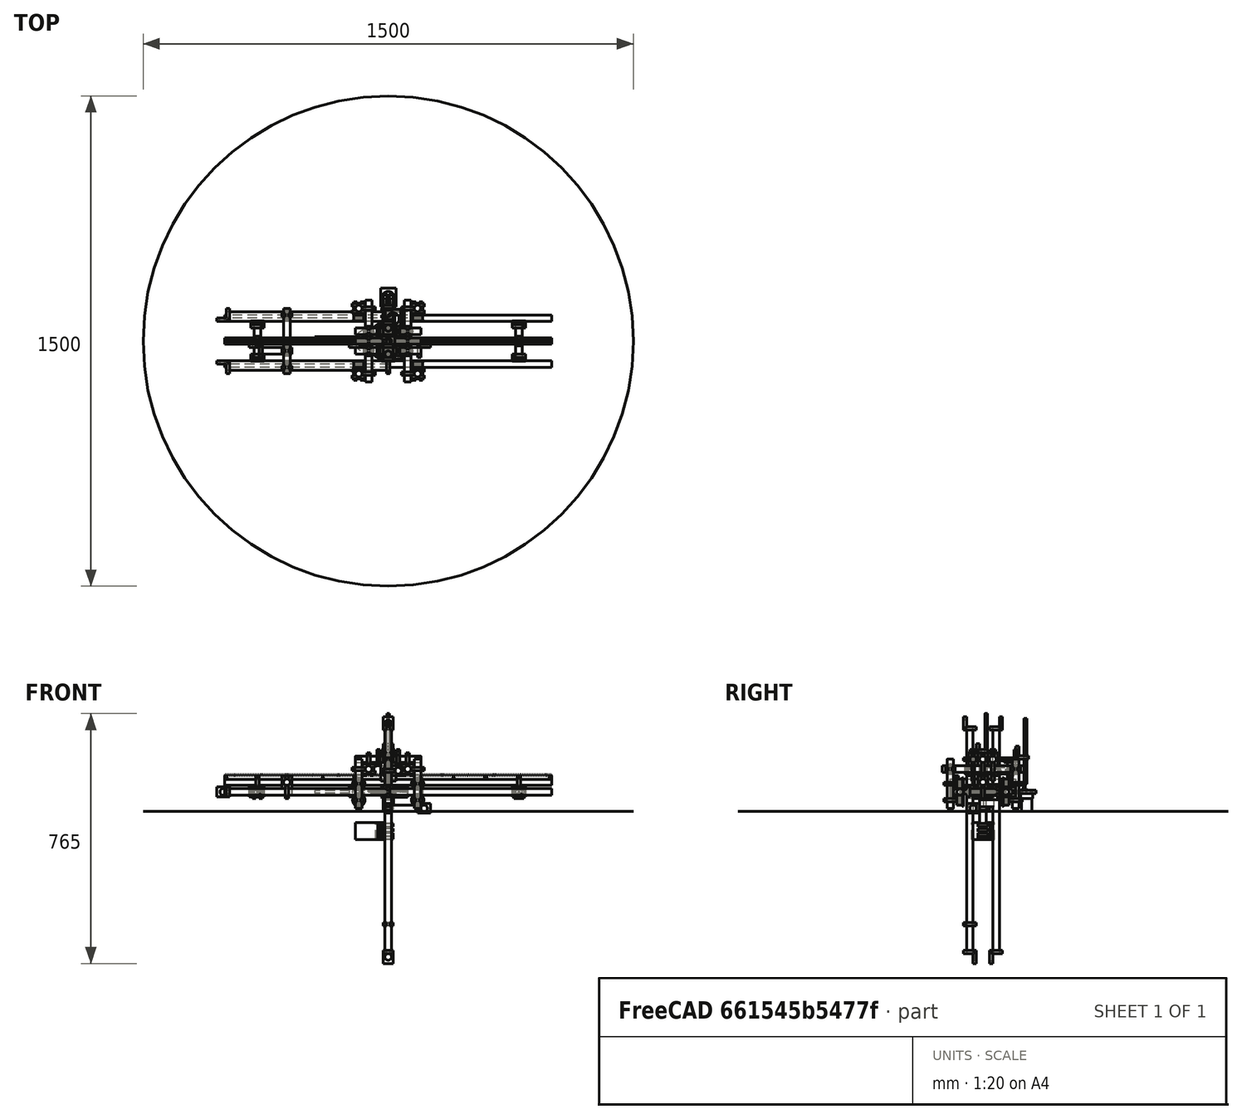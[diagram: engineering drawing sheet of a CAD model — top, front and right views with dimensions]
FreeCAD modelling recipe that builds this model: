
FCSTD DOCUMENT  (FreeCAD 0.17R13522 (Git))
Label: mavis_with_arm_on_1m_rail
License: All rights reserved
LicenseURL: http://en.wikipedia.org/wiki/All_rights_reserved
objects: Part::FeaturePython×50, Part::Cylinder×17, App::DocumentObjectGroup×8, App::Part×8
note: 67 computed .brp shape members not serialized (recipe doc carries the construction recipe); baked Part::Feature solids carry a one-line shape summary decoded from their .brp

FEATURE [Part::FeaturePython] fastener_join_20mm_004  # a2plus imported part (geometry in sourceFile) (typed FeaturePython)
  Placement = pos=(30,-40,65) rot=(0,0.707107,-0.707107;3.14159rad)
  fixedPosition = false
  sourceFile = <userpath>/repo/mavis/parts/fastener-join-20mm.fcstd
  timeLastImport = 1.53614e+09
  updateColors = true
FEATURE [Part::FeaturePython] cogwheel_swivel_01  # a2plus imported part (geometry in sourceFile) (typed FeaturePython)
  fixedPosition = true
  sourceFile = <userpath>/repo/mavis/parts/cogwheel-swivel.fcstd
  timeLastImport = 1.53711e+09
  updateColors = true
FEATURE [Part::FeaturePython] fastener_l_bearing_003  # a2plus imported part (geometry in sourceFile) (typed FeaturePython)
  Placement = pos=(0,-40,195) rot=(0,0,1;1.5708rad)
  fixedPosition = false
  sourceFile = <userpath>/repo/mavis/parts/fastener-l-bearing.fcstd
  timeLastImport = 1.53709e+09
  updateColors = true
FEATURE [Part::FeaturePython] fastener_join_20mm_01  # a2plus imported part (geometry in sourceFile) (typed FeaturePython)
  Placement = pos=(0,85,65) rot=(0,0,1;0rad)
  fixedPosition = false
  sourceFile = <userpath>/repo/mavis/parts/fastener-join-20mm.fcstd
  timeLastImport = 1.53614e+09
  updateColors = true
FEATURE [Part::FeaturePython] fastener_join_20mm_005  # a2plus imported part (geometry in sourceFile) (typed FeaturePython)
  Placement = pos=(30,40,65) rot=(0,0.707107,-0.707107;3.14159rad)
  fixedPosition = false
  sourceFile = <userpath>/repo/mavis/parts/fastener-join-20mm.fcstd
  timeLastImport = 1.53614e+09
  updateColors = true
FEATURE [Part::FeaturePython] fastener_join_20mm_006  # a2plus imported part (geometry in sourceFile) (typed FeaturePython)
  Placement = pos=(0,40,65) rot=(0,0,1;0rad)
  fixedPosition = false
  sourceFile = <userpath>/repo/mavis/parts/fastener-join-20mm.fcstd
  timeLastImport = 1.53614e+09
  updateColors = true
FEATURE [Part::FeaturePython] fastener_l_bearing_005  # a2plus imported part (geometry in sourceFile) (typed FeaturePython)
  Placement = pos=(0,40,195) rot=(0,0,-1;1.5708rad)
  fixedPosition = false
  sourceFile = <userpath>/repo/mavis/parts/fastener-l-bearing.fcstd
  timeLastImport = 1.53709e+09
  updateColors = true
FEATURE [Part::Cylinder] Cylinder003
  Angle = 360
  AttacherType = Attacher::AttachEngine3D
  Height = 200
  Placement = pos=(0,-40,0) rot=(0,0,1;0rad)
  Radius = 10
FEATURE [Part::Cylinder] Cylinder007
  Angle = 360
  AttacherType = Attacher::AttachEngine3D
  Height = 200
  Placement = pos=(0,-40,0) rot=(0,0,1;0rad)
  Radius = 10
FEATURE [Part::Cylinder] Cylinder008
  Angle = 360
  AttacherType = Attacher::AttachEngine3D
  Height = 200
  Placement = pos=(0,40,0) rot=(0,0,1;0rad)
  Radius = 10
FEATURE [Part::Cylinder] Cylinder010
  Angle = 360
  AttacherType = Attacher::AttachEngine3D
  Height = 150
  Placement = pos=(30,-55,65) rot=(-1,0,0;1.5708rad)
  Radius = 10
FEATURE [Part::FeaturePython] fastener_join_20mm_007  # a2plus imported part (geometry in sourceFile) (typed FeaturePython)
  Placement = pos=(0,-40,65) rot=(0,0,1;0rad)
  fixedPosition = false
  sourceFile = <userpath>/repo/mavis/parts/fastener-join-20mm.fcstd
  timeLastImport = 1.53614e+09
  updateColors = true
FEATURE [Part::FeaturePython] fastener_join_20mm_011  # a2plus imported part (geometry in sourceFile) (typed FeaturePython)
  Placement = pos=(30,85,65) rot=(0,0.707107,-0.707107;3.14159rad)
  fixedPosition = false
  sourceFile = <userpath>/repo/mavis/parts/fastener-join-20mm.fcstd
  timeLastImport = 1.53614e+09
  updateColors = true
FEATURE [Part::Cylinder] Cylinder011
  Angle = 360
  AttacherType = Attacher::AttachEngine3D
  Height = 50
  Placement = pos=(0,85,50) rot=(0,0,1;0rad)
  Radius = 10
FEATURE [Part::FeaturePython] fastener_l_bearing_006  # a2plus imported part (geometry in sourceFile) (typed FeaturePython)
  Placement = pos=(0,85,95) rot=(0,0,-1;1.5708rad)
  fixedPosition = false
  sourceFile = <userpath>/repo/mavis/parts/fastener-l-bearing.fcstd
  timeLastImport = 1.53709e+09
  updateColors = true
FEATURE [App::DocumentObjectGroup] Group001  label="BaseParts"
  Group = -> [fastener_l_bearing_006,fastener_join_20mm_011,Cylinder011,Cylinder003,fastener_join_20mm_007,Cylinder010,fastener_l_bearing_005,Cylinder008,fastener_join_20mm_006,fastener_join_20mm_005,Cylinder007,fastener_join_20mm_004,fastener_join_20mm_01,fastener_l_bearing_003,cogwheel_swivel_01]
FEATURE [Part::Cylinder] Cylinder016
  Angle = 360
  AttacherType = Attacher::AttachEngine3D
  Height = 500
  Placement = pos=(5,-80,0) rot=(0,-1,0;1.5708rad)
  Radius = 10
FEATURE [Part::FeaturePython] fastener_m8_20mm_01003  # a2plus imported part (geometry in sourceFile) (typed FeaturePython)
  Placement = pos=(0,80,0) rot=(0.57735,-0.57735,-0.57735;2.0944rad)
  fixedPosition = false
  sourceFile = <userpath>/repo/mavis/parts/fastener-m8-20mm.fcstd
  timeLastImport = 1.53614e+09
  updateColors = true
FEATURE [Part::FeaturePython] fastener_m8_20mm_01004  # a2plus imported part (geometry in sourceFile) (typed FeaturePython)
  Placement = pos=(100,80,0) rot=(0.57735,0.57735,-0.57735;4.18879rad)
  fixedPosition = false
  sourceFile = <userpath>/repo/mavis/parts/fastener-m8-20mm.fcstd
  timeLastImport = 1.53614e+09
  updateColors = true
FEATURE [Part::FeaturePython] fastener_l_bearing_01005  # a2plus imported part (geometry in sourceFile) (typed FeaturePython)
  Placement = pos=(-390,-30,0) rot=(0.57735,-0.57735,-0.57735;2.0944rad)
  fixedPosition = false
  sourceFile = <userpath>/repo/mavis/parts/fastener-l-bearing.fcstd
  timeLastImport = 1.53709e+09
  updateColors = true
FEATURE [Part::Cylinder] Cylinder017
  Angle = 360
  AttacherType = Attacher::AttachEngine3D
  Height = 100
  Placement = pos=(-295,-30,0) rot=(0,-1,0;1.5708rad)
  Radius = 10
FEATURE [Part::Cylinder] Cylinder018
  Angle = 360
  AttacherType = Attacher::AttachEngine3D
  Height = 200
  Placement = pos=(-310,-100,30) rot=(-1,0,0;1.5708rad)
  Radius = 10
FEATURE [Part::FeaturePython] fastener_join_20mm_015  # a2plus imported part (geometry in sourceFile) (typed FeaturePython)
  Placement = pos=(-310,80,0) rot=(0,-1,0;1.5708rad)
  fixedPosition = false
  sourceFile = <userpath>/repo/mavis/parts/fastener-join-20mm.fcstd
  timeLastImport = 1.53614e+09
  updateColors = true
FEATURE [Part::FeaturePython] fastener_join_20mm_016  # a2plus imported part (geometry in sourceFile) (typed FeaturePython)
  Placement = pos=(-310,80,30) rot=(0.57735,0.57735,-0.57735;2.0944rad)
  fixedPosition = false
  sourceFile = <userpath>/repo/mavis/parts/fastener-join-20mm.fcstd
  timeLastImport = 1.53614e+09
  updateColors = true
FEATURE [Part::FeaturePython] fastener_join_20mm_017  # a2plus imported part (geometry in sourceFile) (typed FeaturePython)
  Placement = pos=(-310,-30,30) rot=(0.57735,0.57735,-0.57735;2.0944rad)
  fixedPosition = false
  sourceFile = <userpath>/repo/mavis/parts/fastener-join-20mm.fcstd
  timeLastImport = 1.53614e+09
  updateColors = true
FEATURE [Part::FeaturePython] fastener_join_20mm_018  # a2plus imported part (geometry in sourceFile) (typed FeaturePython)
  Placement = pos=(-310,-30,0) rot=(0.707107,0,0.707107;3.14159rad)
  fixedPosition = false
  sourceFile = <userpath>/repo/mavis/parts/fastener-join-20mm.fcstd
  timeLastImport = 1.53614e+09
  updateColors = true
FEATURE [Part::FeaturePython] fastener_join_20mm_019  # a2plus imported part (geometry in sourceFile) (typed FeaturePython)
  Placement = pos=(-310,-80,0) rot=(0,-1,0;1.5708rad)
  fixedPosition = false
  sourceFile = <userpath>/repo/mavis/parts/fastener-join-20mm.fcstd
  timeLastImport = 1.53614e+09
  updateColors = true
FEATURE [Part::FeaturePython] fastener_join_20mm_020  # a2plus imported part (geometry in sourceFile) (typed FeaturePython)
  Placement = pos=(-310,-80,30) rot=(0.57735,0.57735,-0.57735;2.0944rad)
  fixedPosition = false
  sourceFile = <userpath>/repo/mavis/parts/fastener-join-20mm.fcstd
  timeLastImport = 1.53614e+09
  updateColors = true
FEATURE [Part::FeaturePython] fastener_m8_20mm_01005  # a2plus imported part (geometry in sourceFile) (typed FeaturePython)
  Placement = pos=(0,-80,0) rot=(0.57735,0.57735,-0.57735;4.18879rad)
  fixedPosition = false
  sourceFile = <userpath>/repo/mavis/parts/fastener-m8-20mm.fcstd
  timeLastImport = 1.53614e+09
  updateColors = true
FEATURE [Part::FeaturePython] fastener_l_bearing_01006  # a2plus imported part (geometry in sourceFile) (typed FeaturePython)
  Placement = pos=(-490,80,0) rot=(0.57735,0.57735,-0.57735;4.18879rad)
  fixedPosition = false
  sourceFile = <userpath>/repo/mavis/parts/fastener-l-bearing.fcstd
  timeLastImport = 1.53709e+09
  updateColors = true
FEATURE [Part::FeaturePython] fastener_l_bearing_01007  # a2plus imported part (geometry in sourceFile) (typed FeaturePython)
  Placement = pos=(-490,-80,0) rot=(0.57735,-0.57735,-0.57735;2.0944rad)
  fixedPosition = false
  sourceFile = <userpath>/repo/mavis/parts/fastener-l-bearing.fcstd
  timeLastImport = 1.53709e+09
  updateColors = true
FEATURE [Part::Cylinder] Cylinder019
  Angle = 360
  AttacherType = Attacher::AttachEngine3D
  Height = 600
  Placement = pos=(105,80,0) rot=(0,-1,0;1.5708rad)
  Radius = 10
FEATURE [App::DocumentObjectGroup] Group002  label="ArmParts"
  Group = -> [Cylinder016,fastener_m8_20mm_01003,fastener_m8_20mm_01004,fastener_l_bearing_01005,Cylinder017,Cylinder018,fastener_join_20mm_015,fastener_join_20mm_016,fastener_join_20mm_017,fastener_join_20mm_018,fastener_join_20mm_019,fastener_join_20mm_020,fastener_m8_20mm_01005,fastener_l_bearing_01006,fastener_l_bearing_01007,Cylinder019]
FEATURE [Part::Cylinder] Cylinder020
  Angle = 360
  AttacherType = Attacher::AttachEngine3D
  Height = 500
  Placement = pos=(0,40,5) rot=(0,1,0;3.14159rad)
  Radius = 10
FEATURE [Part::FeaturePython] fastener_m8_20mm_01006  # a2plus imported part (geometry in sourceFile) (typed FeaturePython)
  Placement = pos=(0,-40,100) rot=(0,0,1;1.5708rad)
  fixedPosition = false
  sourceFile = <userpath>/repo/mavis/parts/fastener-m8-20mm.fcstd
  timeLastImport = 1.53614e+09
  updateColors = true
FEATURE [Part::FeaturePython] fastener_m8_20mm_01007  # a2plus imported part (geometry in sourceFile) (typed FeaturePython)
  Placement = pos=(0,-40,0) rot=(0,0,-1;1.5708rad)
  fixedPosition = false
  sourceFile = <userpath>/repo/mavis/parts/fastener-m8-20mm.fcstd
  timeLastImport = 1.53614e+09
  updateColors = true
FEATURE [Part::FeaturePython] fastener_m8_20mm_01008  # a2plus imported part (geometry in sourceFile) (typed FeaturePython)
  Placement = pos=(0,40,0) rot=(0,0,1;1.5708rad)
  fixedPosition = false
  sourceFile = <userpath>/repo/mavis/parts/fastener-m8-20mm.fcstd
  timeLastImport = 1.53614e+09
  updateColors = true
FEATURE [Part::Cylinder] Cylinder021
  Angle = 360
  AttacherType = Attacher::AttachEngine3D
  Height = 600
  Placement = pos=(0,-40,105) rot=(0,1,0;3.14159rad)
  Radius = 10
FEATURE [Part::FeaturePython] fastener_l_bearing_01008  # a2plus imported part (geometry in sourceFile) (typed FeaturePython)
  Placement = pos=(0,40,-490) rot=(0.707107,0.707107,0;3.14159rad)
  fixedPosition = false
  sourceFile = <userpath>/repo/mavis/parts/fastener-l-bearing.fcstd
  timeLastImport = 1.53709e+09
  updateColors = true
FEATURE [Part::FeaturePython] fastener_l_bearing_01009  # a2plus imported part (geometry in sourceFile) (typed FeaturePython)
  Placement = pos=(0,-40,-490) rot=(0.707107,-0.707107,0;3.14159rad)
  fixedPosition = false
  sourceFile = <userpath>/repo/mavis/parts/fastener-l-bearing.fcstd
  timeLastImport = 1.53709e+09
  updateColors = true
FEATURE [Part::FeaturePython] fastener_m8_20mm_01009  # a2plus imported part (geometry in sourceFile) (typed FeaturePython)
  Placement = pos=(0,-40,-405) rot=(0,0,1;1.5708rad)
  fixedPosition = false
  sourceFile = <userpath>/repo/mavis/parts/fastener-m8-20mm.fcstd
  timeLastImport = 1.53614e+09
  updateColors = true
FEATURE [App::DocumentObjectGroup] Group003  label="LowerArmParts"
  Group = -> [Cylinder020,fastener_m8_20mm_01006,fastener_m8_20mm_01007,fastener_m8_20mm_01008,Cylinder021,fastener_l_bearing_01008,fastener_l_bearing_01009,fastener_m8_20mm_01009]
FEATURE [Part::Cylinder] Cylinder022
  Angle = 360
  AttacherType = Attacher::AttachEngine3D
  Height = 150
  Placement = pos=(0,0,-145) rot=(0,0,1;0rad)
  Radius = 10
FEATURE [Part::FeaturePython] fastener_join_20mm_021  # a2plus imported part (geometry in sourceFile) (typed FeaturePython)
  Placement = pos=(0,-30,-50) rot=(0.57735,0.57735,0.57735;2.0944rad)
  fixedPosition = false
  sourceFile = <userpath>/repo/mavis/parts/fastener-join-20mm.fcstd
  timeLastImport = 1.53614e+09
  updateColors = true
FEATURE [Part::FeaturePython] fastener_join_20mm_022  # a2plus imported part (geometry in sourceFile) (typed FeaturePython)
  Placement = pos=(0,0,-50) rot=(0,0,-1;1.5708rad)
  fixedPosition = false
  sourceFile = <userpath>/repo/mavis/parts/fastener-join-20mm.fcstd
  timeLastImport = 1.53614e+09
  updateColors = true
FEATURE [Part::Cylinder] Cylinder023
  Angle = 360
  AttacherType = Attacher::AttachEngine3D
  Height = 110
  Placement = pos=(-10,-30,-50) rot=(0,1,0;1.5708rad)
  Radius = 10
FEATURE [Part::FeaturePython] fastener_l_bearing_01010  # a2plus imported part (geometry in sourceFile) (typed FeaturePython)
  Placement = pos=(95,-30,-50) rot=(0.57735,-0.57735,0.57735;4.18879rad)
  fixedPosition = true
  sourceFile = <userpath>/repo/mavis/parts/fastener-l-bearing.fcstd
  timeLastImport = 1.53709e+09
  updateColors = true
FEATURE [Part::FeaturePython] fastener_m8_double_002  # a2plus imported part (geometry in sourceFile) (typed FeaturePython)
  Placement = pos=(0,0,0) rot=(0,0,1;1.5708rad)
  fixedPosition = false
  sourceFile = <userpath>/repo/mavis/parts/fastener-m8-double.fcstd
  timeLastImport = 1.53754e+09
  updateColors = true
FEATURE [Part::FeaturePython] utm_mount_005  # a2plus imported part (geometry in sourceFile) (typed FeaturePython)
  Placement = pos=(0,0,-140) rot=(0,0,1;0rad)
  fixedPosition = false
  sourceFile = <userpath>/repo/mavis/parts/utm-mount.fcstd
  timeLastImport = 1.53754e+09
  updateColors = true
FEATURE [Part::FeaturePython] utm_mount_006  # a2plus imported part (geometry in sourceFile) (typed FeaturePython)
  Placement = pos=(0,0,-101) rot=(0,0,1;0rad)
  fixedPosition = false
  sourceFile = <userpath>/repo/mavis/parts/utm-mount.fcstd
  timeLastImport = 1.53754e+09
  updateColors = true
FEATURE [Part::FeaturePython] utm_mount_007  # a2plus imported part (geometry in sourceFile) (typed FeaturePython)
  Placement = pos=(0,0,-116) rot=(0,0,1;0rad)
  fixedPosition = false
  sourceFile = <userpath>/repo/mavis/parts/utm-mount.fcstd
  timeLastImport = 1.53754e+09
  updateColors = true
FEATURE [Part::FeaturePython] utm_mount_008  # a2plus imported part (geometry in sourceFile) (typed FeaturePython)
  Placement = pos=(0,0,-130) rot=(0,0,1;0rad)
  fixedPosition = false
  sourceFile = <userpath>/repo/mavis/parts/utm-mount.fcstd
  timeLastImport = 1.53754e+09
  updateColors = true
FEATURE [Part::FeaturePython] DC_Gear_Motor_37mm_004  # a2plus imported part (geometry in sourceFile) (typed FeaturePython)
  Placement = pos=(0,133.5,-60) rot=(0,0,-1;1.5708rad)
  fixedPosition = false
  sourceFile = <userpath>/.FreeCAD/Mod/parts_library/Electrical Parts/Motors/DC_Gear_Motor_37mm.fcstd
  timeLastImport = 1.53685e+09
  updateColors = true
FEATURE [Part::FeaturePython] fastener_l_bearing_nut_004  # a2plus imported part (geometry in sourceFile) (typed FeaturePython)
  Placement = pos=(0,120,120.4) rot=(0,0,1;1.5708rad)
  fixedPosition = false
  sourceFile = <userpath>/repo/mavis/parts/fastener-l-bearing-nut.fcstd
  timeLastImport = 1.53675e+09
  updateColors = true
FEATURE [Part::FeaturePython] fastener_join_37mm_005  # a2plus imported part (geometry in sourceFile) (typed FeaturePython)
  Placement = pos=(0,115,0) rot=(0,0,1;1.5708rad)
  fixedPosition = false
  sourceFile = <userpath>/repo/mavis/parts/fastener-join-37mm.fcstd
  timeLastImport = 1.53614e+09
  updateColors = true
FEATURE [Part::Cylinder] Cylinder024
  Angle = 360
  AttacherType = Attacher::AttachEngine3D
  Height = 200
  Placement = pos=(0,130,25) rot=(0,0,1;0rad)
  Radius = 4
FEATURE [App::DocumentObjectGroup] Group005  label="ArmSwivelParts"
  Group = -> [DC_Gear_Motor_37mm_004,fastener_l_bearing_nut_004,fastener_join_37mm_005,Cylinder024]
FEATURE [App::Part] Part003  label="ArmSwivel"
  Group = -> [Group005,DC_Gear_Motor_37mm_004,fastener_l_bearing_nut_004,fastener_join_37mm_005,Cylinder024]
  License = CC BY 3.0
  LicenseURL = http://creativecommons.org/licenses/by/3.0/
  Origin = -> Origin009
  Placement = pos=(0,0,110) rot=(0,-1,0;5.35816rad)
FEATURE [Part::FeaturePython] fastener_join_37mm_006  # a2plus imported part (geometry in sourceFile) (typed FeaturePython)
  Placement = pos=(0,0,0) rot=(0.57735,0.57735,0.57735;2.0944rad)
  fixedPosition = false
  sourceFile = <userpath>/repo/mavis/parts/fastener-join-37mm.fcstd
  timeLastImport = 1.53614e+09
  updateColors = true
FEATURE [Part::FeaturePython] DC_Gear_Motor_37mm_005  # a2plus imported part (geometry in sourceFile) (typed FeaturePython)
  Placement = pos=(60,18.5,0) rot=(0.57735,-0.57735,-0.57735;2.0944rad)
  fixedPosition = false
  sourceFile = <userpath>/.FreeCAD/Mod/parts_library/Electrical Parts/Motors/DC_Gear_Motor_37mm.fcstd
  timeLastImport = 1.53685e+09
  updateColors = true
FEATURE [Part::FeaturePython] fastener_l_bearing_nut_005  # a2plus imported part (geometry in sourceFile) (typed FeaturePython)
  Placement = pos=(-99,0,0) rot=(0.57735,0.57735,-0.57735;4.18879rad)
  fixedPosition = false
  sourceFile = <userpath>/repo/mavis/parts/fastener-l-bearing-nut.fcstd
  timeLastImport = 1.53675e+09
  updateColors = true
FEATURE [Part::Cylinder] Cylinder025
  Angle = 360
  AttacherType = Attacher::AttachEngine3D
  Height = 200
  Placement = pos=(-25,10,0) rot=(0,-1,0;1.5708rad)
  Radius = 4
FEATURE [App::DocumentObjectGroup] Group006  label="LowerArmSwivelParts"
  Group = -> [fastener_join_37mm_006,DC_Gear_Motor_37mm_005,fastener_l_bearing_nut_005,Cylinder025]
FEATURE [App::Part] Part004  label="LowerArmSwivel"
  Group = -> [DC_Gear_Motor_37mm_005,fastener_l_bearing_nut_005,fastener_join_37mm_006,Group006,Cylinder025]
  License = CC BY 3.0
  LicenseURL = http://creativecommons.org/licenses/by/3.0/
  Origin = -> Origin010
  Placement = pos=(-405,0,0) rot=(0,1,0;1.03847rad)
FEATURE [Part::FeaturePython] fastener_join_37mm_007  # a2plus imported part (geometry in sourceFile) (typed FeaturePython)
  Placement = pos=(0,0,0) rot=(0,0,1;1.5708rad)
  fixedPosition = false
  sourceFile = <userpath>/repo/mavis/parts/fastener-join-37mm.fcstd
  timeLastImport = 1.53614e+09
  updateColors = true
FEATURE [Part::FeaturePython] fastener_l_bearing_nut_006  # a2plus imported part (geometry in sourceFile) (typed FeaturePython)
  Placement = pos=(0,0,128) rot=(0,0,1;1.5708rad)
  fixedPosition = false
  sourceFile = <userpath>/repo/mavis/parts/fastener-l-bearing-nut.fcstd
  timeLastImport = 1.53675e+09
  updateColors = true
FEATURE [Part::FeaturePython] DC_Gear_Motor_37mm_006  # a2plus imported part (geometry in sourceFile) (typed FeaturePython)
  Placement = pos=(0,18.5,-45) rot=(0,0,-1;1.5708rad)
  fixedPosition = false
  sourceFile = <userpath>/.FreeCAD/Mod/parts_library/Electrical Parts/Motors/DC_Gear_Motor_37mm.fcstd
  timeLastImport = 1.53685e+09
  updateColors = true
FEATURE [Part::Cylinder] Cylinder026
  Angle = 360
  AttacherType = Attacher::AttachEngine3D
  Height = 200
  Placement = pos=(0,10,40) rot=(0,0,1;0rad)
  Radius = 4
FEATURE [App::DocumentObjectGroup] Group007  label="TipSwivelParts"
  Group = -> [fastener_join_37mm_007,fastener_l_bearing_nut_006,DC_Gear_Motor_37mm_006,Cylinder026]
FEATURE [App::Part] Part005  label="TipSwivel"
  Group = -> [fastener_l_bearing_nut_006,Cylinder026,DC_Gear_Motor_37mm_006,fastener_join_37mm_007,Group007]
  License = CC BY 3.0
  LicenseURL = http://creativecommons.org/licenses/by/3.0/
  Origin = -> Origin011
  Placement = pos=(110,0,-50) rot=(0,-1,0;0.314159rad)
FEATURE [Part::FeaturePython] utm_mock_01  # a2plus imported part (geometry in sourceFile) (typed FeaturePython)
  Placement = pos=(-66,0,-146) rot=(0,0,1;0rad)
  fixedPosition = false
  sourceFile = <userpath>/repo/mavis/assemblies/utm-mock.fcstd
  timeLastImport = 1.53769e+09
  updateColors = true
FEATURE [App::DocumentObjectGroup] Group004  label="TipParts"
  Group = -> [Cylinder022,fastener_join_20mm_021,fastener_join_20mm_022,Cylinder023,fastener_l_bearing_01010,fastener_m8_double_002,utm_mount_005,utm_mount_006,utm_mount_007,utm_mount_008,utm_mock_01]
FEATURE [App::Part] Part002  label="Tip"
  Group = -> [utm_mount_008,utm_mount_007,Cylinder022,Cylinder023,fastener_join_20mm_021,fastener_join_20mm_022,utm_mount_006,utm_mount_005,fastener_l_bearing_01010,fastener_m8_double_002,Group004,Part005,utm_mock_01]
  License = CC BY 3.0
  LicenseURL = http://creativecommons.org/licenses/by/3.0/
  Origin = -> Origin008
  Placement = pos=(0,0,-505) rot=(0,1,0;5.49779rad)
FEATURE [App::Part] Part001  label="LowerArm"
  Group = -> [Group003,Cylinder020,fastener_m8_20mm_01006,fastener_m8_20mm_01007,fastener_m8_20mm_01008,Cylinder021,fastener_l_bearing_01008,fastener_l_bearing_01009,fastener_m8_20mm_01009,Part002]
  License = CC BY 3.0
  LicenseURL = http://creativecommons.org/licenses/by/3.0/
  Origin = -> Origin007
  Placement = pos=(-505,0,0) rot=(0,-1,0;5.75959rad)
FEATURE [App::Part] Part  label="Arm"
  Group = -> [Group002,Cylinder016,fastener_m8_20mm_01003,fastener_m8_20mm_01004,fastener_l_bearing_01005,Cylinder017,Cylinder018,fastener_join_20mm_015,fastener_join_20mm_016,fastener_join_20mm_017,fastener_join_20mm_018,fastener_join_20mm_019,fastener_join_20mm_020,fastener_m8_20mm_01005,fastener_l_bearing_01006,fastener_l_bearing_01007,Cylinder019,Part001,Part004]
  License = CC BY 3.0
  LicenseURL = http://creativecommons.org/licenses/by/3.0/
  Origin = -> Origin006
  Placement = pos=(0,0,210) rot=(0,-1,0;6.02139rad)
FEATURE [Part::FeaturePython] mavis_01  # a2plus imported part (geometry in sourceFile) (typed FeaturePython)
  fixedPosition = false
  sourceFile = <userpath>/repo/mavis/assemblies/mavis.fcstd
  timeLastImport = 1.53769e+09
  updateColors = true
FEATURE [App::Part] Part006  label="ArmAssembly"
  Group = -> [Cylinder011,fastener_join_20mm_004,fastener_join_20mm_01,Cylinder003,fastener_join_20mm_011,fastener_l_bearing_003,fastener_join_20mm_006,Cylinder008,Cylinder007,fastener_join_20mm_007,fastener_join_20mm_005,fastener_l_bearing_006,fastener_l_bearing_005,Cylinder010,cogwheel_swivel_01,Group001,Part,Part003]
  License = CC BY 3.0
  LicenseURL = http://creativecommons.org/licenses/by/3.0/
  Origin = -> Origin
  Placement = pos=(0,0,136) rot=(0,0,1;4.71239rad)
FEATURE [App::Part] Part007  label="MavisWithArm"
  Group = -> [mavis_01,Part006]
  License = CC BY 3.0
  LicenseURL = http://creativecommons.org/licenses/by/3.0/
  Origin = -> Origin012
FEATURE [Part::FeaturePython] rail_01  # a2plus imported part (geometry in sourceFile) (typed FeaturePython)
  fixedPosition = false
  sourceFile = <userpath>/repo/mavis/assemblies/rail.fcstd
  timeLastImport = 1.53614e+09
  updateColors = true
FEATURE [Part::Cylinder] Cylinder  label="Ground"
  Angle = 360
  AttacherType = Attacher::AttachEngine3D
  Height = 1
  Placement = pos=(0,0,-60) rot=(0,0,1;0rad)
  Radius = 750
FEATURE [Part::FeaturePython] RaytracingCamera  # WARN: FeaturePython — macro-defined, semantics opaque (R4)
  Placement = pos=(1500,-1500,750) rot=(0,0,1;0rad)
FEATURE [Part::FeaturePython] RaytracingTarget  # WARN: FeaturePython — macro-defined, semantics opaque (R4)
  Placement = pos=(-100,0,300) rot=(0,0,1;0rad)
FEATURE [App::DocumentObjectGroup] Raytracing
  Group = -> [RaytracingCamera,RaytracingTarget]
